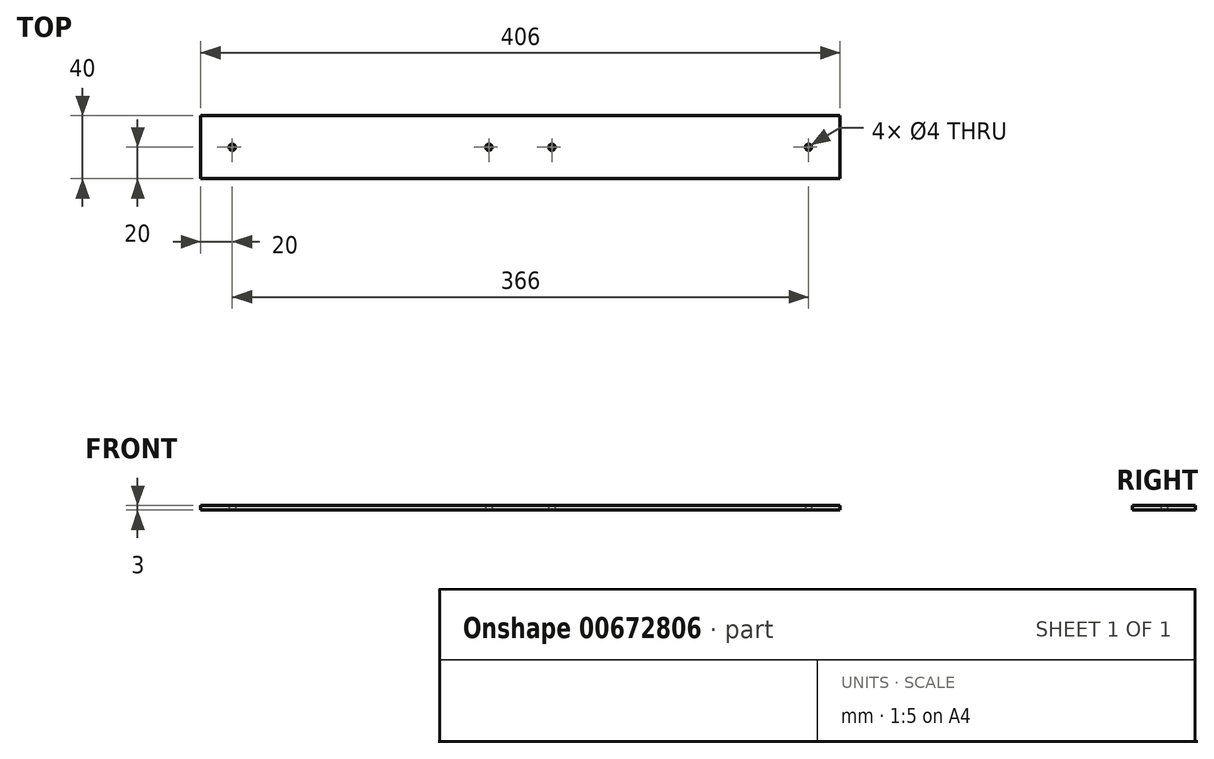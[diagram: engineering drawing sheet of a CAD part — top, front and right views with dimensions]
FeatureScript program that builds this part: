
annotation { "Feature Type Name" : "Feature", "Feature Type Description" : "" }
export const myFeature = defineFeature(function(context is Context, id is Id, definition is map)
    precondition{}
    {
        {
            var Q0;
            Q0=qCreatedBy(makeId("Top.planeOp"),FACE);
            var sketch = newSketch(context, id + "F0", { "sketchPlane" : qUnion([Q0])});
            skLineSegment(sketch, "E0.bottom", {"start": v(-203, 20) * mm, "end": v(203, 20) * mm});
            skLineSegment(sketch, "E0.top", {"start": v(-203, -20) * mm, "end": v(203, -20) * mm});
            skLineSegment(sketch, "E0.left", {"start": v(-203, 20) * mm, "end": v(-203, -20) * mm});
            skLineSegment(sketch, "E0.right", {"start": v(203, 20) * mm, "end": v(203, -20) * mm});
            skPoint(sketch, "E0.middle", {"position": v(0, 0) * mm});
            skCircle(sketch, "E1", {"center": v(-20, 0) * mm, "radius": 2 * mm});
            skCircle(sketch, "E2", {"center": v(20, 0) * mm, "radius": 2 * mm});
            skLineSegment(sketch, "E3", {"start": v(-20, 0) * mm, "end": v(20, 0) * mm});
            skCircle(sketch, "E4", {"center": v(-183, 0) * mm, "radius": 2 * mm});
            skCircle(sketch, "E5", {"center": v(183, 0) * mm, "radius": 2 * mm});
            skSolve(sketch);
        }
        {
            var Q0;
            Q0=makeQuery(id+"F0.imprint","IMPRINT",FACE,{"disambiguationData":[TD([[makeQuery(id+"F0.imprint","IMPRINT",EDGE,{"derivedFrom":sQuery(id+"F0.wireOp",EDGE,"E0.bottom")}),-1.0]])]});
            extrude(context, id + "F1", {"entities" : qUnion([Q0]), "depth" : 3 * mm, "offsetDistance" : 25 * mm});
        }
    });
